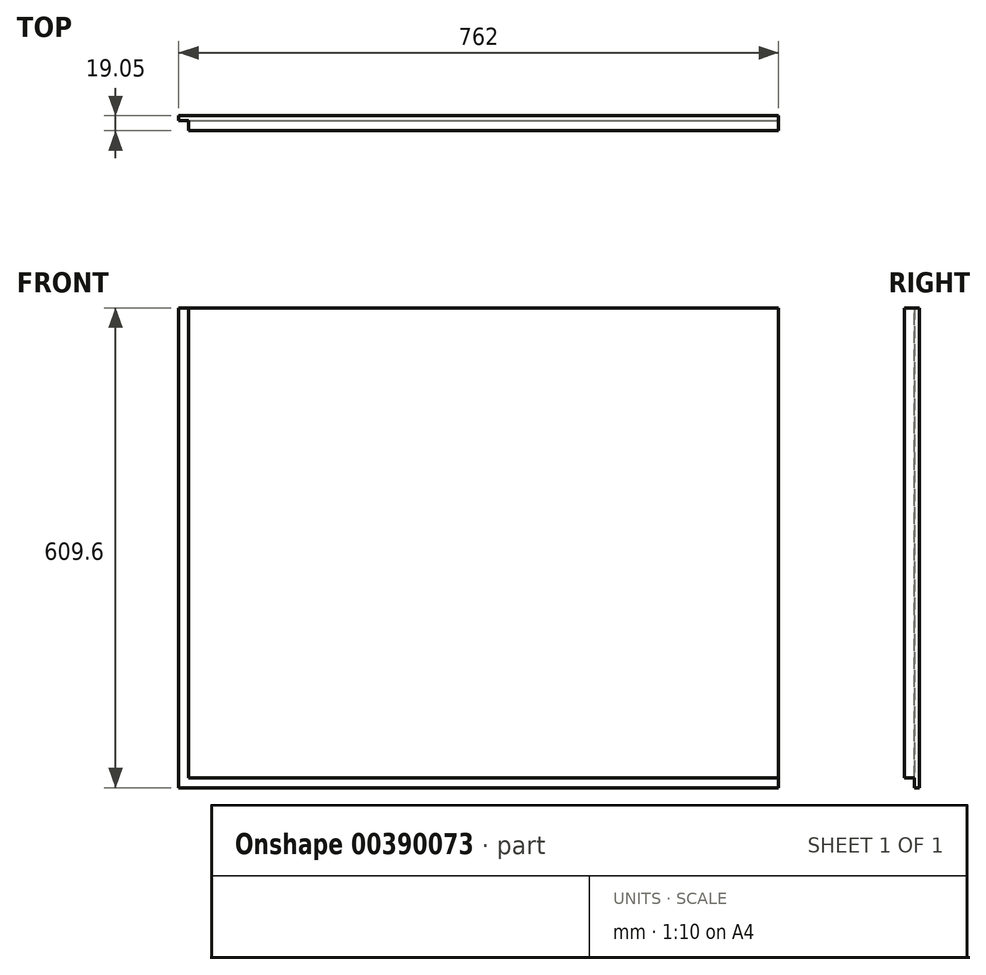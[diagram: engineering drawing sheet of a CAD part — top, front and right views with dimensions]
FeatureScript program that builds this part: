
annotation { "Feature Type Name" : "Feature", "Feature Type Description" : "" }
export const myFeature = defineFeature(function(context is Context, id is Id, definition is map)
    precondition{}
    {
        {
            var Q0;
            Q0=qCreatedBy(makeId("Front.planeOp"),FACE);
            var sketch = newSketch(context, id + "F0", { "sketchPlane" : qUnion([Q0])});
            skLineSegment(sketch, "E0.bottom", {"start": v(0, 0) * mm, "end": v(762, 0) * mm});
            skLineSegment(sketch, "E0.top", {"start": v(0, 609.6) * mm, "end": v(762, 609.6) * mm});
            skLineSegment(sketch, "E0.left", {"start": v(0, 0) * mm, "end": v(0, 609.6) * mm});
            skLineSegment(sketch, "E0.right", {"start": v(762, 0) * mm, "end": v(762, 609.6) * mm});
            skSolve(sketch);
        }
        {
            var Q0;
            Q0=makeQuery(id+"F0.imprint","IMPRINT",FACE,{"disambiguationData":[TD([[makeQuery(id+"F0.imprint","IMPRINT",EDGE,{"derivedFrom":sQuery(id+"F0.wireOp",EDGE,"E0.bottom")}),1.0]])]});
            extrude(context, id + "F1", {"entities" : qUnion([Q0]), "depth" : 19.05 * mm});
        }
        {
            var Q0;
            Q0=makeQuery(id+"F1.opExtrude","SWEPT_FACE",FACE,{"disambiguationData":[OSD([sQuery(id+"F0.wireOp",EDGE,"E0.right")])]});
            var sketch = newSketch(context, id + "F2", { "sketchPlane" : qUnion([Q0])});
            skLineSegment(sketch, "E1", {"start": v(-19.05, 0) * mm, "end": v(-6.35, 0) * mm});
            skLineSegment(sketch, "E2", {"start": v(-6.35, 0) * mm, "end": v(-6.35, 12.8) * mm});
            skLineSegment(sketch, "E3", {"start": v(-6.35, 12.8) * mm, "end": v(-19.05, 12.8) * mm});
            skLineSegment(sketch, "E4", {"start": v(-19.05, 12.8) * mm, "end": v(-19.05, 0) * mm});
            skSolve(sketch);
        }
        {
            var Q0;
            Q0=makeQuery(id+"F2.imprint","IMPRINT",FACE,{"disambiguationData":[TD([[makeQuery(id+"F2.imprint","IMPRINT",EDGE,{"derivedFrom":sQuery(id+"F2.wireOp",EDGE,"E1")}),1.0]])]});
            extrude(context, id + "F3", {"entities" : qUnion([Q0]), "operationType" : NewBodyOperationType.REMOVE, "endBound" : BoundingType.THROUGH_ALL, "oppositeDirection" : true, "depth" : 30.48 * mm});
        }
        {
            var Q0;
            Q0=makeQuery(id+"F1.opExtrude","SWEPT_FACE",FACE,{"disambiguationData":[OSD([sQuery(id+"F0.wireOp",EDGE,"E0.top")])]});
            var sketch = newSketch(context, id + "F4", { "sketchPlane" : qUnion([Q0])});
            skLineSegment(sketch, "E5", {"start": v(0, -19.05) * mm, "end": v(12.7, -19.05) * mm});
            skLineSegment(sketch, "E6", {"start": v(12.7, -19.05) * mm, "end": v(12.7, -6.35) * mm});
            skLineSegment(sketch, "E7", {"start": v(12.7, -6.35) * mm, "end": v(0, -6.35) * mm});
            skLineSegment(sketch, "E8", {"start": v(0, -6.35) * mm, "end": v(0, -19.05) * mm});
            skSolve(sketch);
        }
        {
            var Q0;
            Q0=makeQuery(id+"F4.imprint","IMPRINT",FACE,{"disambiguationData":[TD([[makeQuery(id+"F4.imprint","IMPRINT",EDGE,{"derivedFrom":sQuery(id+"F4.wireOp",EDGE,"E5")}),1.0]])]});
            extrude(context, id + "F5", {"entities" : qUnion([Q0]), "operationType" : NewBodyOperationType.REMOVE, "endBound" : BoundingType.THROUGH_ALL, "oppositeDirection" : true, "depth" : 25.4 * mm});
        }
    });
